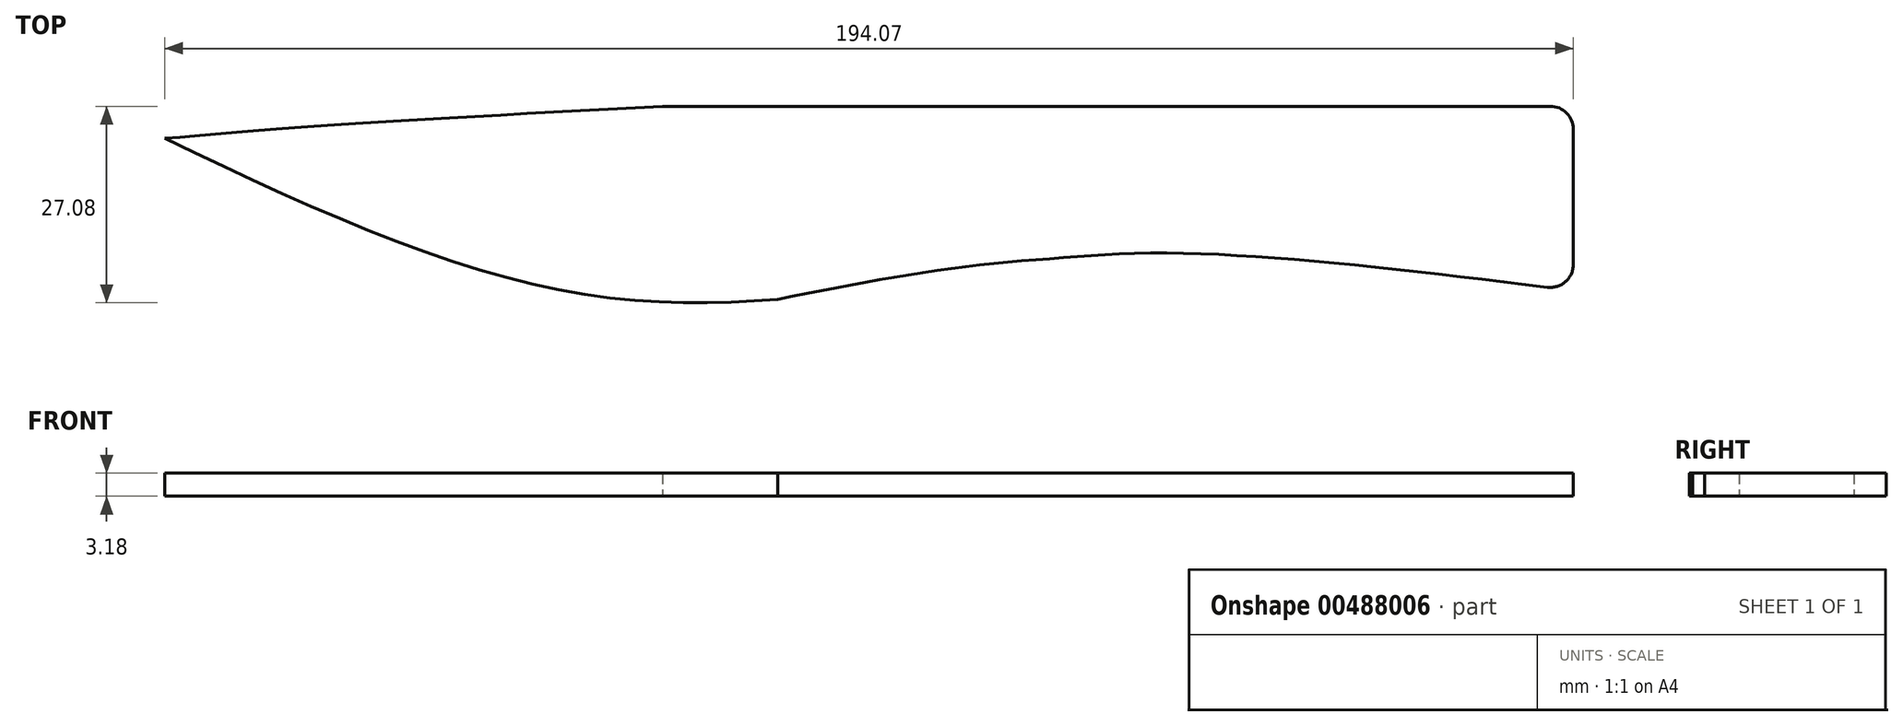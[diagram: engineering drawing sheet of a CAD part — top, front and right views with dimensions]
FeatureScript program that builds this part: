
annotation { "Feature Type Name" : "Feature", "Feature Type Description" : "" }
export const myFeature = defineFeature(function(context is Context, id is Id, definition is map)
    precondition{}
    {
        {
            var Q0;
            Q0=qCreatedBy(makeId("Top.planeOp"),FACE);
            var sketch = newSketch(context, id + "F0", { "sketchPlane" : qUnion([Q0])});
            skLineSegment(sketch, "E0.top", {"start": v(-3.18, 25.4) * mm, "end": v(-125.45, 25.4) * mm});
            skLineSegment(sketch, "E0.left", {"start": v(0, 3.6) * mm, "end": v(0, 22.23) * mm});
            skFitSpline(sketch, "E1", {"points": [v(-203.2, 25.4) * mm, v(-139.3, 0) * mm, v(-97.12, 0) * mm], "startDerivative": vector(118.96, -58) * mm, "endDerivative": vector(92.12, 9.95) * mm});
            skFitSpline(sketch, "E2", {"points": [v(-86.53, 0) * mm, v(-64.53, 4.92) * mm, v(0, 0) * mm], "startDerivative": vector(51.24, 17.16) * mm, "endDerivative": vector(116.24, -14.45) * mm});
            skPoint(sketch, "E3.visualSharp", {"position": v(0, 25.4) * mm});
            skArc(sketch, "E3.filletArc", {"start": v(0, 22.23) * mm, "mid": v(-0.93, 24.47) * mm, "end": v(-3.18, 25.4) * mm});
            skArc(sketch, "E4.filletArc", {"start": v(-3.57, 0.44) * mm, "mid": v(-1.07, 1.21) * mm, "end": v(0, 3.6) * mm});
            skFitSpline(sketch, "E5", {"points": [v(-125.45, 25.4) * mm, v(-172.92, 22.68) * mm, v(-194.07, 20.96) * mm], "startDerivative": vector(-87.07, -4.64) * mm, "endDerivative": vector(-47.49, -4.1) * mm});
            skPoint(sketch, "E6.2.internal.orphan", {"position": v(-64.53, 6.41) * mm});
            skFitSpline(sketch, "E7", {"points": [v(-109.61, -1.22) * mm, v(-86.12, 2.98) * mm, v(-64.53, 4.92) * mm], "startDerivative": vector(46.31, 9.27) * mm, "endDerivative": vector(43.84, 2.95) * mm});
            skSolve(sketch);
        }
        {
            var Q0;
            Q0 = qSketchRegion(id + "F0", true);
            var sketch = newSketch(context, id + "F1", { "sketchPlane" : qUnion([Q0])});
            skSolve(sketch);
        }
        {
            var Q0;
            Q0=makeQuery(id+"F1.imprint","IMPRINT",FACE,{"disambiguationData":[TD([[makeQuery(id+"F1.imprint","IMPRINT",EDGE,{"derivedFrom":makeQuery(id+"F0.imprint","IMPRINT",EDGE,{"derivedFrom":sQuery(id+"F0.wireOp",EDGE,"E0.top")})}),1.0]])]});
            extrude(context, id + "F2", {"entities" : qUnion([Q0]), "depth" : 3.17 * mm});
        }
    });
